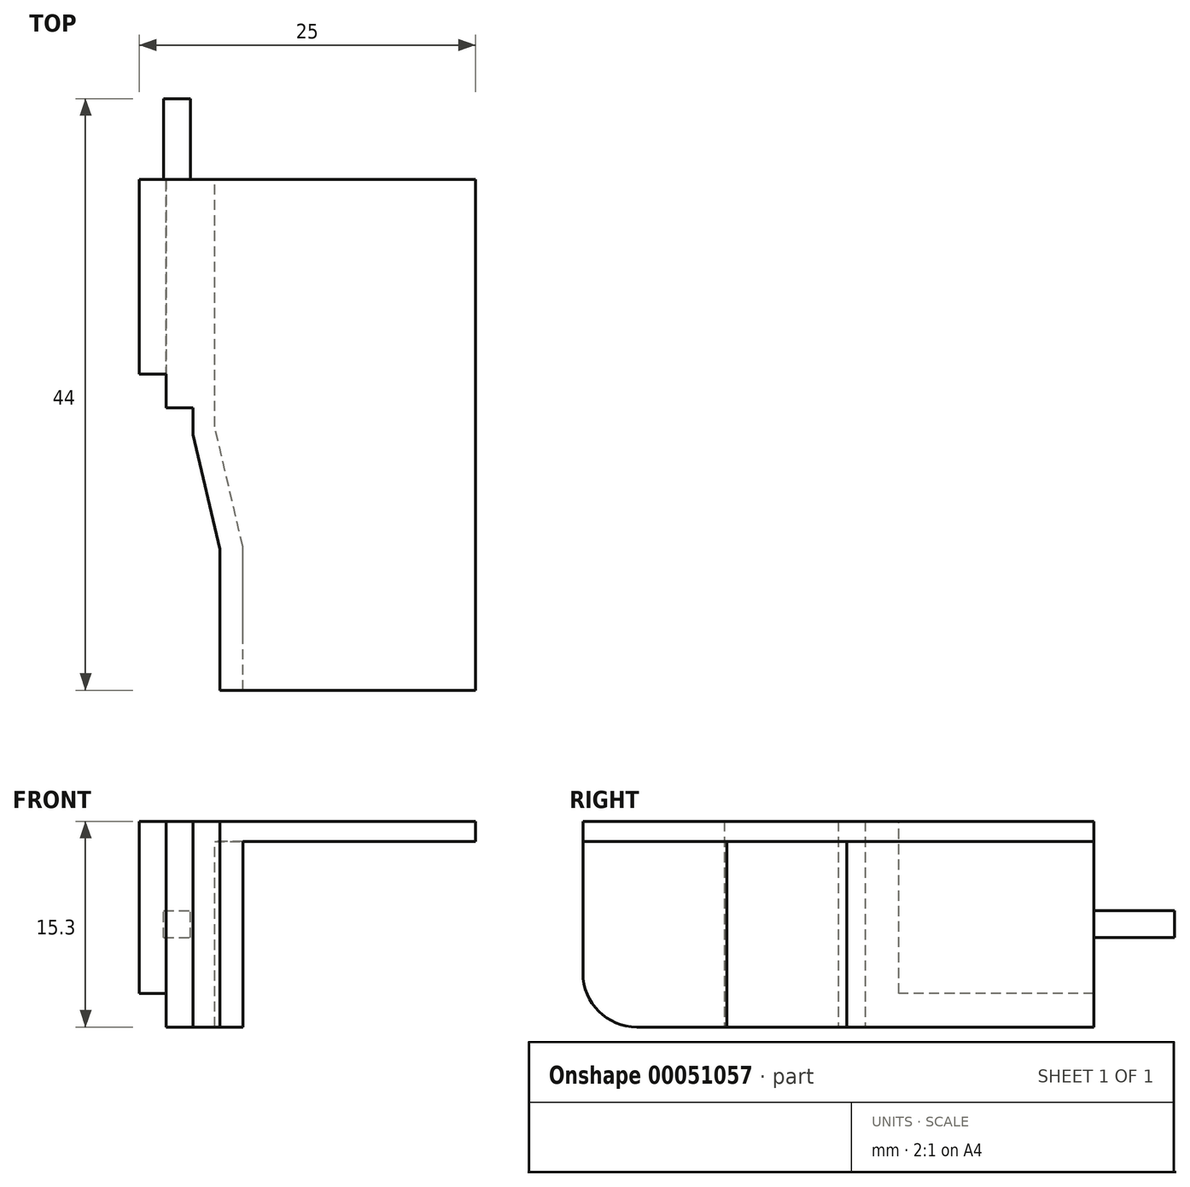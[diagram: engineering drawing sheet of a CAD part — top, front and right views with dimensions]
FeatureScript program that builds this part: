
annotation { "Feature Type Name" : "Feature", "Feature Type Description" : "" }
export const myFeature = defineFeature(function(context is Context, id is Id, definition is map)
    precondition{}
    {
        {
            var Q0;
            Q0=qCreatedBy(makeId("Top.planeOp"),FACE);
            var sketch = newSketch(context, id + "F0", { "sketchPlane" : qUnion([Q0])});
            skLineSegment(sketch, "E0", {"start": v(-20.56, 14.84) * mm, "end": v(2.44, 14.84) * mm});
            skLineSegment(sketch, "E1", {"start": v(2.44, 14.84) * mm, "end": v(2.44, -23.16) * mm});
            skLineSegment(sketch, "E2", {"start": v(2.44, -23.16) * mm, "end": v(-16.56, -23.16) * mm});
            skLineSegment(sketch, "E3", {"start": v(-16.56, -23.16) * mm, "end": v(-16.56, -12.66) * mm});
            skLineSegment(sketch, "E4", {"start": v(-20.56, -2.16) * mm, "end": v(-18.56, -2.16) * mm});
            skLineSegment(sketch, "E5", {"start": v(-20.56, -2.16) * mm, "end": v(-20.56, 14.84) * mm});
            skLineSegment(sketch, "E6", {"start": v(-18.56, -2.16) * mm, "end": v(-18.56, -4.16) * mm});
            skLineSegment(sketch, "E7", {"start": v(-18.56, -4.16) * mm, "end": v(-16.56, -12.66) * mm});
            skSolve(sketch);
        }
        {
            var Q0;
            Q0=makeQuery(id+"F0.imprint","IMPRINT",FACE,{"disambiguationData":[TD([[makeQuery(id+"F0.imprint","IMPRINT",EDGE,{"derivedFrom":sQuery(id+"F0.wireOp",EDGE,"E0")}),-1.0]])]});
            extrude(context, id + "F1", {"entities" : qUnion([Q0]), "depth" : 1.5 * mm});
        }
        {
            var Q0;
            Q0=makeQuery(id+"F1.opExtrude","CAP_FACE",FACE,{"disambiguationData":[OSD([sQuery(id+"F0.wireOp",EDGE,"E0"),sQuery(id+"F0.wireOp",EDGE,"E1"),sQuery(id+"F0.wireOp",EDGE,"E2"),sQuery(id+"F0.wireOp",EDGE,"E3"),sQuery(id+"F0.wireOp",EDGE,"85047c72-3e91-40ef-aa9c-166d9a1c90d9"),sQuery(id+"F0.wireOp",EDGE,"E4"),sQuery(id+"F0.wireOp",EDGE,"E5")])],"isStart":true});
            var sketch = newSketch(context, id + "F2", { "sketchPlane" : qUnion([Q0])});
            skLineSegment(sketch, "E8", {"start": v(-16.56, 23.16) * mm, "end": v(-14.86, 23.16) * mm});
            skLineSegment(sketch, "E9", {"start": v(-14.86, 23.16) * mm, "end": v(-14.86, 12.46) * mm});
            skLineSegment(sketch, "E10", {"start": v(-14.86, 12.46) * mm, "end": v(-16.96, 3.54) * mm});
            skLineSegment(sketch, "E11", {"start": v(-16.96, 3.54) * mm, "end": v(-16.96, -14.84) * mm});
            skLineSegment(sketch, "E12", {"start": v(-16.96, -14.84) * mm, "end": v(-20.56, -14.84) * mm});
            skLineSegment(sketch, "E13", {"start": v(-20.56, -14.84) * mm, "end": v(-20.56, 2.16) * mm});
            skLineSegment(sketch, "E14", {"start": v(-20.56, 2.16) * mm, "end": v(-18.56, 2.16) * mm});
            skLineSegment(sketch, "E15", {"start": v(-18.56, 2.16) * mm, "end": v(-18.56, 4.16) * mm});
            skLineSegment(sketch, "E16", {"start": v(-18.56, 4.16) * mm, "end": v(-16.56, 12.66) * mm});
            skLineSegment(sketch, "E17", {"start": v(-16.56, 12.66) * mm, "end": v(-16.56, 23.16) * mm});
            skSolve(sketch);
        }
        {
            var Q0;
            Q0=makeQuery(id+"F2.imprint","IMPRINT",FACE,{"disambiguationData":[TD([[makeQuery(id+"F2.imprint","IMPRINT",EDGE,{"derivedFrom":sQuery(id+"F2.wireOp",EDGE,"E8")}),1.0]])]});
            extrude(context, id + "F3", {"entities" : qUnion([Q0]), "operationType" : NewBodyOperationType.ADD, "depth" : 13.8 * mm});
        }
        {
            var Q0;
            Q0=makeQuery(id+"F3.boolean.opBoolean","MERGE",FACE,{"derivedFrom":[makeQuery(id+"F1.opExtrude","SWEPT_FACE",FACE,{"disambiguationData":[OSD([sQuery(id+"F0.wireOp",EDGE,"E5")])]}),makeQuery(id+"F3.opExtrude","SWEPT_FACE",FACE,{"disambiguationData":[OSD([sQuery(id+"F2.wireOp",EDGE,"E13")])]})]});
            var sketch = newSketch(context, id + "F4", { "sketchPlane" : qUnion([Q0])});
            skLineSegment(sketch, "E18", {"start": v(-14.84, -11.3) * mm, "end": v(-0.34, -11.3) * mm});
            skLineSegment(sketch, "E19", {"start": v(-0.34, -11.3) * mm, "end": v(-0.34, 1.5) * mm});
            skLineSegment(sketch, "E20", {"start": v(-0.34, 1.5) * mm, "end": v(-14.84, 1.5) * mm});
            skLineSegment(sketch, "E21", {"start": v(-14.84, 1.5) * mm, "end": v(-14.84, -11.3) * mm});
            skSolve(sketch);
        }
        {
            var Q0;
            Q0=makeQuery(id+"F4.imprint","IMPRINT",FACE,{"disambiguationData":[TD([[makeQuery(id+"F4.imprint","IMPRINT",EDGE,{"derivedFrom":sQuery(id+"F4.wireOp",EDGE,"E18")}),1.0]])]});
            extrude(context, id + "F5", {"entities" : qUnion([Q0]), "operationType" : NewBodyOperationType.ADD, "depth" : 2 * mm});
        }
        {
            var Q0;
            Q0=makeQuery(id+"F5.boolean.opBoolean","MERGE",FACE,{"derivedFrom":[makeQuery(id+"F3.boolean.opBoolean","MERGE",FACE,{"derivedFrom":[makeQuery(id+"F1.opExtrude","SWEPT_FACE",FACE,{"disambiguationData":[OSD([sQuery(id+"F0.wireOp",EDGE,"E0")])]}),makeQuery(id+"F3.opExtrude","SWEPT_FACE",FACE,{"disambiguationData":[OSD([sQuery(id+"F2.wireOp",EDGE,"E12")])]})]}),makeQuery(id+"F5.opExtrude","SWEPT_FACE",FACE,{"disambiguationData":[OSD([sQuery(id+"F4.wireOp",EDGE,"E21")])]})]});
            var sketch = newSketch(context, id + "F6", { "sketchPlane" : qUnion([Q0])});
            skLineSegment(sketch, "E22", {"start": v(19.76, 2.24) * mm, "end": v(19.76, -15.27) * mm, "construction": true});
            skLineSegment(sketch, "E23", {"start": v(8.55, -6.15) * mm, "end": v(27.37, -6.15) * mm, "construction": true});
            skLineSegment(sketch, "E24.rect.bottom", {"start": v(20.76, -7.15) * mm, "end": v(18.76, -7.15) * mm});
            skLineSegment(sketch, "E24.rect.top", {"start": v(20.76, -5.15) * mm, "end": v(18.76, -5.15) * mm});
            skLineSegment(sketch, "E24.rect.left", {"start": v(20.76, -7.15) * mm, "end": v(20.76, -5.15) * mm});
            skLineSegment(sketch, "E24.rect.right", {"start": v(18.76, -7.15) * mm, "end": v(18.76, -5.15) * mm});
            skPoint(sketch, "E24.rect.middle", {"position": v(19.76, -6.15) * mm});
            skSolve(sketch);
        }
        {
            var Q0;
            Q0=makeQuery(id+"F6.imprint","IMPRINT",FACE,{"disambiguationData":[TD([[makeQuery(id+"F6.imprint","IMPRINT",EDGE,{"derivedFrom":sQuery(id+"F6.wireOp",EDGE,"E24.rect.bottom")}),-1.0]])]});
            extrude(context, id + "F7", {"entities" : qUnion([Q0]), "operationType" : NewBodyOperationType.ADD, "depth" : 6 * mm});
        }
        {
            var Q0;
            Q0=makeQuery(id+"F3.opExtrude","CAP_EDGE",EDGE,{"disambiguationData":[OSD([sQuery(id+"F2.wireOp",EDGE,"E8")])],"isStart":false});
            fillet(context, id + "F8", {"entities" : qUnion([Q0]), "radius" : 4 * mm, "tangentPropagation" : true, "allowEdgeOverflow" : false});
        }
    });
